FCSTD DOCUMENT  (FreeCAD 0.21R33771 (Git))
Label: unshielded_multiwire
License: All rights reserved
LicenseURL: https://en.wikipedia.org/wiki/All_rights_reserved
objects: Part::Part2DObjectPython×3
note: 3 computed .brp shape members not serialized (recipe doc carries the construction recipe); baked Part::Feature solids carry a one-line shape summary decoded from their .brp

FEATURE [Part::Part2DObjectPython] Circle  label="Conductor_0"  # Draft 2D object (typed FeaturePython)
  Area = 314.159
  FirstAngle = 0
  LastAngle = 0
  MakeFace = true
  Placement = pos=(-10,0,0) rot=(0,0,1;0rad)
  Radius = 10
FEATURE [Part::Part2DObjectPython] Circle001  label="Conductor_1"  # Draft 2D object (typed FeaturePython)
  Area = 78.5398
  FirstAngle = 0
  LastAngle = 0
  MakeFace = true
  Placement = pos=(10,0,0) rot=(0,0,1;0rad)
  Radius = 5
FEATURE [Part::Part2DObjectPython] Circle002  label="Dielectric_1"  # Draft 2D object (typed FeaturePython)
  Area = 176.715
  FirstAngle = 0
  LastAngle = 0
  MakeFace = true
  Placement = pos=(10,0,0) rot=(0,0,1;0rad)
  Radius = 7.5
